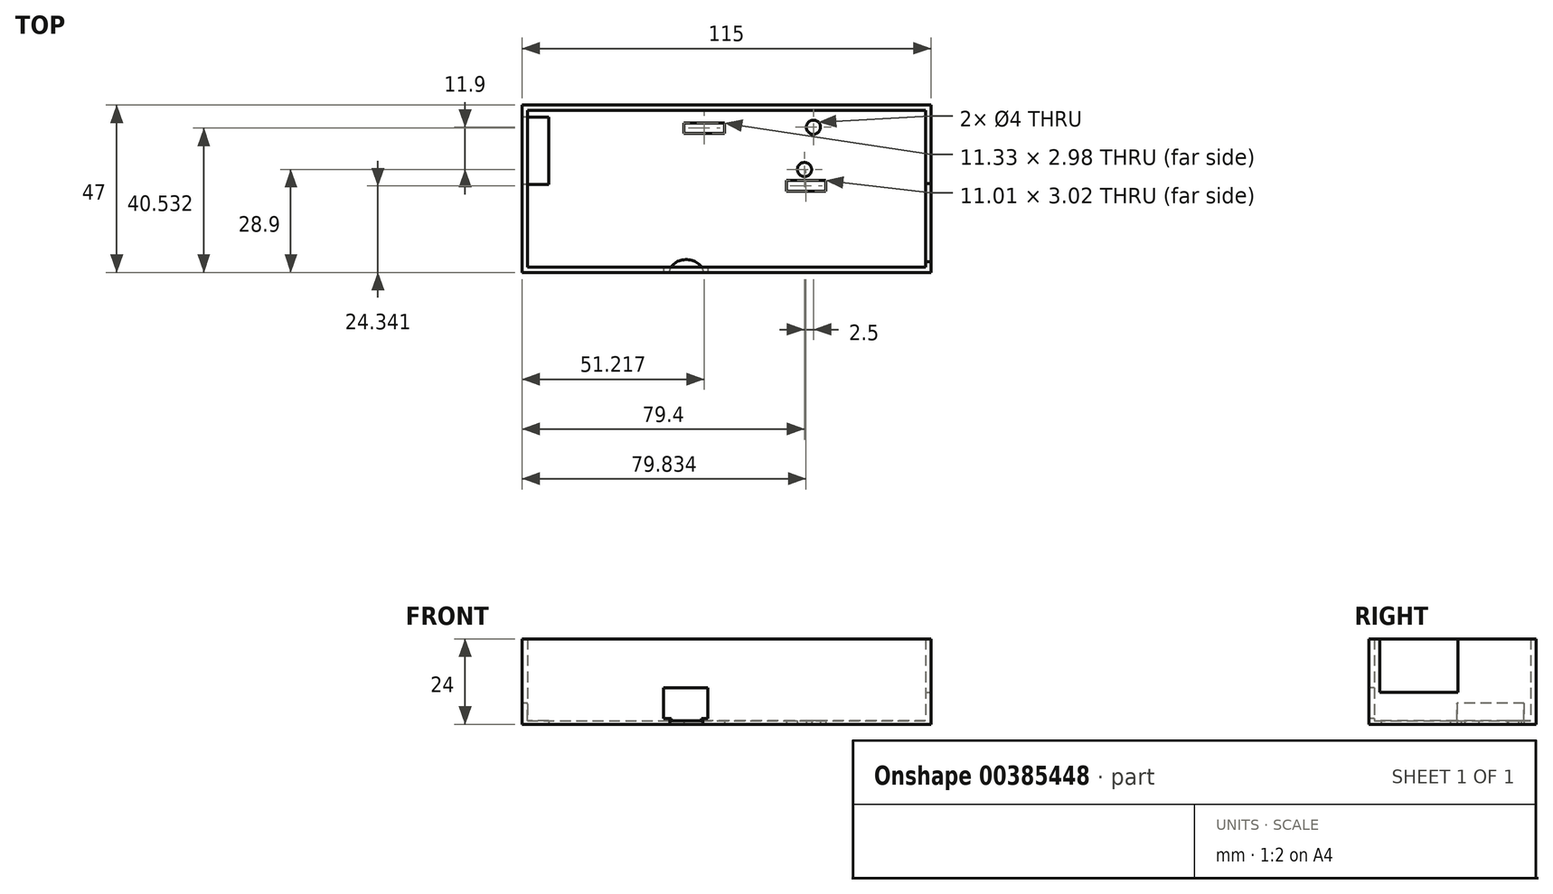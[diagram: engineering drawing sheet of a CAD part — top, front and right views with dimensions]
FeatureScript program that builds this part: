
annotation { "Feature Type Name" : "Feature", "Feature Type Description" : "" }
export const myFeature = defineFeature(function(context is Context, id is Id, definition is map)
    precondition{}
    {
        {
            var Q0;
            Q0=qCreatedBy(makeId("Top.planeOp"),FACE);
            var sketch = newSketch(context, id + "F0", { "sketchPlane" : qUnion([Q0])});
            skLineSegment(sketch, "E0.bottom", {"start": v(56, -22) * mm, "end": v(-56, -22) * mm});
            skLineSegment(sketch, "E0.top", {"start": v(56, 22) * mm, "end": v(-56, 22) * mm});
            skLineSegment(sketch, "E0.left", {"start": v(56, -22) * mm, "end": v(56, 22) * mm});
            skLineSegment(sketch, "E0.right", {"start": v(-56, -22) * mm, "end": v(-56, 22) * mm});
            skPoint(sketch, "E0.middle", {"position": v(0, 0) * mm});
            skLineSegment(sketch, "E1.0", {"start": v(57.5, 23.5) * mm, "end": v(-57.5, 23.5) * mm});
            skLineSegment(sketch, "E1.1", {"start": v(57.5, -23.5) * mm, "end": v(57.5, 23.5) * mm});
            skLineSegment(sketch, "E1.2", {"start": v(57.5, -23.5) * mm, "end": v(-57.5, -23.5) * mm});
            skLineSegment(sketch, "E1.3", {"start": v(-57.5, -23.5) * mm, "end": v(-57.5, 23.5) * mm});
            skSolve(sketch);
        }
        {
            var Q0;
            Q0=makeQuery(id+"F0.imprint","IMPRINT",FACE,{"disambiguationData":[TD([[makeQuery(id+"F0.imprint","IMPRINT",EDGE,{"derivedFrom":sQuery(id+"F0.wireOp",EDGE,"E0.bottom")}),-1.0]])]});
            var Q1;
            Q1=makeQuery(id+"F0.imprint","IMPRINT",FACE,{"disambiguationData":[TD([[makeQuery(id+"F0.imprint","IMPRINT",EDGE,{"derivedFrom":sQuery(id+"F0.wireOp",EDGE,"E0.bottom")}),1.0]])]});
            extrude(context, id + "F1", {"entities" : qUnion([Q0, Q1]), "depth" : 1 * mm});
        }
        {
            var Q0;
            Q0=makeQuery(id+"F1.opExtrude","CAP_FACE",FACE,{"disambiguationData":[OSD([sQuery(id+"F0.wireOp",EDGE,"E1.0"),sQuery(id+"F0.wireOp",EDGE,"E1.1"),sQuery(id+"F0.wireOp",EDGE,"E1.2"),sQuery(id+"F0.wireOp",EDGE,"E1.3")])],"isStart":false});
            var sketch = newSketch(context, id + "F2", { "sketchPlane" : qUnion([Q0])});
            skLineSegment(sketch, "E2.0", {"start": v(-56, 22) * mm, "end": v(-56, -22) * mm});
            skLineSegment(sketch, "E2.1", {"start": v(56, 22) * mm, "end": v(-56, 22) * mm});
            skLineSegment(sketch, "E2.2", {"start": v(56, -22) * mm, "end": v(56, 22) * mm});
            skLineSegment(sketch, "E2.3", {"start": v(-56, -22) * mm, "end": v(56, -22) * mm});
            skSolve(sketch);
        }
        {
            var Q0;
            Q0=makeQuery(id+"F2.imprint","IMPRINT",FACE,{"disambiguationData":[TD([[makeQuery(id+"F2.imprint","IMPRINT",EDGE,{"derivedFrom":sQuery(id+"F2.wireOp",EDGE,"E2.0")}),-1.0]])]});
            extrude(context, id + "F3", {"entities" : qUnion([Q0]), "operationType" : NewBodyOperationType.ADD, "depth" : 8 * mm});
        }
        {
            var Q0;
            Q0=makeQuery(id+"F3.opExtrude","CAP_FACE",FACE,{"disambiguationData":[OSD([sQuery(id+"F0.wireOp",EDGE,"E1.0"),sQuery(id+"F0.wireOp",EDGE,"E1.1"),sQuery(id+"F0.wireOp",EDGE,"E1.2"),sQuery(id+"F0.wireOp",EDGE,"E1.3"),sQuery(id+"F2.wireOp",EDGE,"E2.0"),sQuery(id+"F2.wireOp",EDGE,"E2.1"),sQuery(id+"F2.wireOp",EDGE,"E2.2"),sQuery(id+"F2.wireOp",EDGE,"E2.3")])],"isStart":false});
            var sketch = newSketch(context, id + "F4", { "sketchPlane" : qUnion([Q0])});
            skLineSegment(sketch, "E3", {"start": v(56, -20.5) * mm, "end": v(57.5, -20.5) * mm});
            skLineSegment(sketch, "E4", {"start": v(56, 1.5) * mm, "end": v(57.5, 1.5) * mm});
            skSolve(sketch);
        }
        {
            var Q0;
            {var subQ2=sQuery(id+"F4.wireOp",EDGE,"E3");Q0=makeQuery(id+"F4.imprint","IMPRINT",FACE,{"disambiguationData":[TD([[makeQuery(id+"F4.imprint","IMPRINT",EDGE,{"derivedFrom":subQ2}),-1.0]])]});}
            extrude(context, id + "F5", {"entities" : qUnion([Q0]), "operationType" : NewBodyOperationType.ADD, "depth" : 15 * mm});
        }
        {
            var Q0;
            Q0=makeQuery(id+"F1.opExtrude","CAP_FACE",FACE,{"disambiguationData":[OSD([sQuery(id+"F0.wireOp",EDGE,"E1.0"),sQuery(id+"F0.wireOp",EDGE,"E1.1"),sQuery(id+"F0.wireOp",EDGE,"E1.2"),sQuery(id+"F0.wireOp",EDGE,"E1.3")])],"isStart":true});
            var sketch = newSketch(context, id + "F6", { "sketchPlane" : qUnion([Q0])});
            skCircle(sketch, "E5", {"center": v(24.4, -17.3) * mm, "radius": 2 * mm});
            skCircle(sketch, "E6", {"center": v(21.9, -5.4) * mm, "radius": 2 * mm});
            skLineSegment(sketch, "E7.bottom", {"start": v(27.84, -2.35) * mm, "end": v(16.83, -2.35) * mm});
            skLineSegment(sketch, "E7.top", {"start": v(27.84, 0.67) * mm, "end": v(16.83, 0.67) * mm});
            skLineSegment(sketch, "E7.left", {"start": v(27.84, -2.35) * mm, "end": v(27.84, 0.67) * mm});
            skLineSegment(sketch, "E7.right", {"start": v(16.83, -2.35) * mm, "end": v(16.83, 0.67) * mm});
            skPoint(sketch, "E7.middle", {"position": v(22.33, -0.84) * mm});
            skLineSegment(sketch, "E8.bottom", {"start": v(-0.62, -15.54) * mm, "end": v(-11.95, -15.54) * mm});
            skLineSegment(sketch, "E8.top", {"start": v(-0.62, -18.52) * mm, "end": v(-11.95, -18.52) * mm});
            skLineSegment(sketch, "E8.left", {"start": v(-0.62, -15.54) * mm, "end": v(-0.62, -18.52) * mm});
            skLineSegment(sketch, "E8.right", {"start": v(-11.95, -15.54) * mm, "end": v(-11.95, -18.52) * mm});
            skPoint(sketch, "E8.middle", {"position": v(-6.28, -17.03) * mm});
            skSolve(sketch);
        }
        {
            var Q0;
            Q0=makeQuery(id+"F6.imprint","IMPRINT",FACE,{"disambiguationData":[TD([[makeQuery(id+"F6.imprint","IMPRINT",EDGE,{"derivedFrom":sQuery(id+"F6.wireOp",EDGE,"E5")}),1.0]])]});
            var Q1;
            Q1=makeQuery(id+"F6.imprint","IMPRINT",FACE,{"disambiguationData":[TD([[makeQuery(id+"F6.imprint","IMPRINT",EDGE,{"derivedFrom":sQuery(id+"F6.wireOp",EDGE,"E6")}),1.0]])]});
            var Q2;
            Q2=makeQuery(id+"F6.imprint","IMPRINT",FACE,{"disambiguationData":[TD([[makeQuery(id+"F6.imprint","IMPRINT",EDGE,{"derivedFrom":sQuery(id+"F6.wireOp",EDGE,"E7.bottom")}),-1.0]])]});
            var Q3;
            Q3=makeQuery(id+"F6.imprint","IMPRINT",FACE,{"disambiguationData":[TD([[makeQuery(id+"F6.imprint","IMPRINT",EDGE,{"derivedFrom":sQuery(id+"F6.wireOp",EDGE,"04acb3bf-7fc4-43a7-9a21-acaa3ffd717e.bottom")}),-1.0]])]});
            var Q4;
            Q4=makeQuery(id+"F6.imprint","IMPRINT",FACE,{"disambiguationData":[TD([[makeQuery(id+"F6.imprint","IMPRINT",EDGE,{"derivedFrom":sQuery(id+"F6.wireOp",EDGE,"E8.bottom")}),1.0]])]});
            var Q5;
            Q5=sQuery(id+"F6.wireOp",EDGE,"E5");
            extrude(context, id + "F7", {"entities" : qUnion([Q0, Q1, Q2, Q3, Q4]), "operationType" : NewBodyOperationType.REMOVE, "surfaceEntities" : qUnion([Q5]), "oppositeDirection" : true, "depth" : 5 * mm});
        }
        {
            var Q0;
            {var subQ0=sQuery(id+"F0.wireOp",EDGE,"E1.2");Q0=makeQuery(id+"F5.boolean.opBoolean","MERGE",FACE,{"derivedFrom":[makeQuery(id+"F3.boolean.opBoolean","MERGE",FACE,{"derivedFrom":[makeQuery(id+"F1.opExtrude","SWEPT_FACE",FACE,{"disambiguationData":[OSD([subQ0])]}),makeQuery(id+"F3.opExtrude","SWEPT_FACE",FACE,{"disambiguationData":[OSD([subQ0])]})]}),makeQuery(id+"F5.opExtrude","SWEPT_FACE",FACE,{"disambiguationData":[OSD([subQ0])]})]});}
            var sketch = newSketch(context, id + "F8", { "sketchPlane" : qUnion([Q0])});
            skLineSegment(sketch, "E9.bottom", {"start": v(-5.34, 1.58) * mm, "end": v(-17.73, 1.58) * mm});
            skLineSegment(sketch, "E9.top", {"start": v(-5.34, 10.28) * mm, "end": v(-17.73, 10.28) * mm});
            skLineSegment(sketch, "E9.left", {"start": v(-5.34, 1.58) * mm, "end": v(-5.34, 10.28) * mm});
            skLineSegment(sketch, "E9.right", {"start": v(-17.73, 1.58) * mm, "end": v(-17.73, 10.28) * mm});
            skPoint(sketch, "E9.middle", {"position": v(-11.53, 5.93) * mm});
            skSolve(sketch);
        }
        {
            var Q0;
            Q0=makeQuery(id+"F8.imprint","IMPRINT",FACE,{"disambiguationData":[TD([[makeQuery(id+"F8.imprint","IMPRINT",EDGE,{"derivedFrom":sQuery(id+"F8.wireOp",EDGE,"E9.bottom")}),-1.0]])]});
            extrude(context, id + "F9", {"entities" : qUnion([Q0]), "operationType" : NewBodyOperationType.REMOVE, "oppositeDirection" : true, "depth" : 5 * mm});
        }
        {
            var Q0;
            Q0=makeQuery(id+"F1.opExtrude","CAP_FACE",FACE,{"disambiguationData":[OSD([sQuery(id+"F0.wireOp",EDGE,"E1.0"),sQuery(id+"F0.wireOp",EDGE,"E1.1"),sQuery(id+"F0.wireOp",EDGE,"E1.2"),sQuery(id+"F0.wireOp",EDGE,"E1.3")])],"isStart":true});
            var sketch = newSketch(context, id + "F10", { "sketchPlane" : qUnion([Q0])});
            skEllipse(sketch, "E10", {"center": v(-11.32, 23.5) * mm, "majorRadius": 4.66 * mm, "minorRadius": 3.6 * mm, "majorAxis": v(1, 0)});
            skSolve(sketch);
        }
        {
            var Q0;
            {var subQ0=sQuery(id+"F0.wireOp",EDGE,"E1.3");Q0=makeQuery(id+"F5.boolean.opBoolean","MERGE",FACE,{"derivedFrom":[makeQuery(id+"F3.boolean.opBoolean","MERGE",FACE,{"derivedFrom":[makeQuery(id+"F1.opExtrude","SWEPT_FACE",FACE,{"disambiguationData":[OSD([subQ0])]}),makeQuery(id+"F3.opExtrude","SWEPT_FACE",FACE,{"disambiguationData":[OSD([subQ0])]})]}),makeQuery(id+"F5.opExtrude","SWEPT_FACE",FACE,{"disambiguationData":[OSD([subQ0])]})]});}
            var sketch = newSketch(context, id + "F11", { "sketchPlane" : qUnion([Q0])});
            skLineSegment(sketch, "E11.bottom", {"start": v(-20.08, 5.87) * mm, "end": v(-1.22, 5.87) * mm});
            skLineSegment(sketch, "E11.top", {"start": v(-20.08, -0.73) * mm, "end": v(-1.22, -0.73) * mm});
            skLineSegment(sketch, "E11.left", {"start": v(-20.08, 5.87) * mm, "end": v(-20.08, -0.73) * mm});
            skLineSegment(sketch, "E11.right", {"start": v(-1.22, 5.87) * mm, "end": v(-1.22, -0.73) * mm});
            skPoint(sketch, "E11.middle", {"position": v(-10.65, 2.57) * mm});
            skSolve(sketch);
        }
        {
            var Q0;
            Q0=makeQuery(id+"F11.imprint","IMPRINT",FACE,{"disambiguationData":[TD([[makeQuery(id+"F11.imprint","IMPRINT",EDGE,{"derivedFrom":sQuery(id+"F11.wireOp",EDGE,"E11.bottom")}),-1.0]])]});
            extrude(context, id + "F12", {"entities" : qUnion([Q0]), "operationType" : NewBodyOperationType.REMOVE, "oppositeDirection" : true, "depth" : 7.5 * mm});
        }
        {
            var Q0;
            {var subQ0=sQuery(id+"F0.wireOp",EDGE,"E1.1");var subQ1=makeQuery(id+"F3.opExtrude","CAP_EDGE",EDGE,{"disambiguationData":[OSD([subQ0])],"isStart":false});Q0=makeQuery(id+"F5.boolean.opBoolean","MERGE",FACE,{"derivedFrom":[makeQuery(id+"F3.boolean.opBoolean","MERGE",FACE,{"derivedFrom":[makeQuery(id+"F1.opExtrude","SWEPT_FACE",FACE,{"disambiguationData":[OSD([subQ0])]}),makeQuery(id+"F3.opExtrude","SWEPT_FACE",FACE,{"disambiguationData":[OSD([subQ0])]})]}),makeQuery(id+"F5.opExtrude","SWEPT_FACE",FACE,{"disambiguationData":[OSD([subQ0]),TDD([makeQuery(id+"F4.imprint","IMPRINT",EDGE,{"disambiguationData":[TD([[makeQuery(id+"F4.imprint","INTERSECT",VERTEX,{"derivedFrom":[makeQuery(id+"F3.opExtrude","CAP_EDGE",EDGE,{"disambiguationData":[OSD([sQuery(id+"F0.wireOp",EDGE,"E1.0")])],"isStart":false}),subQ1]}),1.0]])],"derivedFrom":subQ1})])]}),makeQuery(id+"F5.opExtrude","SWEPT_FACE",FACE,{"disambiguationData":[OSD([subQ0]),TDD([makeQuery(id+"F4.imprint","IMPRINT",EDGE,{"disambiguationData":[TD([[makeQuery(id+"F4.imprint","INTERSECT",VERTEX,{"derivedFrom":[subQ1,makeQuery(id+"F3.opExtrude","CAP_EDGE",EDGE,{"disambiguationData":[OSD([sQuery(id+"F0.wireOp",EDGE,"E1.2")])],"isStart":false})]}),-1.0]])],"derivedFrom":subQ1})])]})]});}
            var sketch = newSketch(context, id + "F13", { "sketchPlane" : qUnion([Q0])});
            skLineSegment(sketch, "E12.bottom", {"start": v(-20.1, 11) * mm, "end": v(1.27, 11) * mm});
            skLineSegment(sketch, "E12.top", {"start": v(-20.1, 9) * mm, "end": v(1.27, 9) * mm});
            skLineSegment(sketch, "E12.left", {"start": v(-20.1, 11) * mm, "end": v(-20.1, 9) * mm});
            skLineSegment(sketch, "E12.right", {"start": v(1.27, 11) * mm, "end": v(1.27, 9) * mm});
            skSolve(sketch);
        }
        {
            var Q0;
            {var subQ0=sQuery(id+"F13.wireOp",EDGE,"E12.bottom");var subQ1=sQuery(id+"F0.wireOp",EDGE,"E1.1");var subQ2=makeQuery(id+"F5.opExtrude","SWEPT_EDGE",EDGE,{"disambiguationData":[OSD([subQ1,sQuery(id+"F4.wireOp",EDGE,"E3")])]});var subQ3=makeQuery(id+"F13.imprint","INTERSECT",VERTEX,{"derivedFrom":[subQ2,subQ0]});Q0=makeQuery(id+"F13.imprint","IMPRINT",FACE,{"disambiguationData":[TD([[makeQuery(id+"F13.imprint","IMPRINT",EDGE,{"disambiguationData":[TD([[subQ3,-1.0]])],"derivedFrom":subQ0}),-1.0]])]});}
            var Q1;
            {var subQ0=sQuery(id+"F13.wireOp",EDGE,"E12.right");Q1=makeQuery(id+"F13.imprint","IMPRINT",FACE,{"disambiguationData":[TD([[makeQuery(id+"F13.imprint","IMPRINT",EDGE,{"derivedFrom":subQ0}),-1.0]])]});}
            var Q2;
            {var subQ0=sQuery(id+"F13.wireOp",EDGE,"E12.left");Q2=makeQuery(id+"F13.imprint","IMPRINT",FACE,{"disambiguationData":[TD([[makeQuery(id+"F13.imprint","IMPRINT",EDGE,{"derivedFrom":subQ0}),1.0]])]});}
            extrude(context, id + "F14", {"entities" : qUnion([Q0, Q1, Q2]), "operationType" : NewBodyOperationType.REMOVE, "oppositeDirection" : true, "depth" : 5 * mm});
        }
        {
            var Q0;
            {var subQ0=sQuery(id+"F10.wireOp",EDGE,"E10");var subQ1=makeQuery(id+"F1.opExtrude","CAP_EDGE",EDGE,{"disambiguationData":[OSD([sQuery(id+"F0.wireOp",EDGE,"E1.2")])],"isStart":true});var subQ2=makeQuery(id+"F10.imprint","INTERSECT",VERTEX,{"disambiguationData":[OD(0.0)],"derivedFrom":[subQ1,subQ0]});Q0=makeQuery(id+"F10.imprint","IMPRINT",FACE,{"disambiguationData":[TD([[makeQuery(id+"F10.imprint","IMPRINT",EDGE,{"disambiguationData":[TD([[subQ2,1.0]])],"derivedFrom":subQ0}),1.0]])]});}
            var Q1;
            Q1=sQuery(id+"F10.wireOp",EDGE,"E10");
            extrude(context, id + "F15", {"entities" : qUnion([Q0]), "operationType" : NewBodyOperationType.REMOVE, "surfaceEntities" : qUnion([Q1]), "oppositeDirection" : true, "depth" : 4 * mm});
        }
    });
